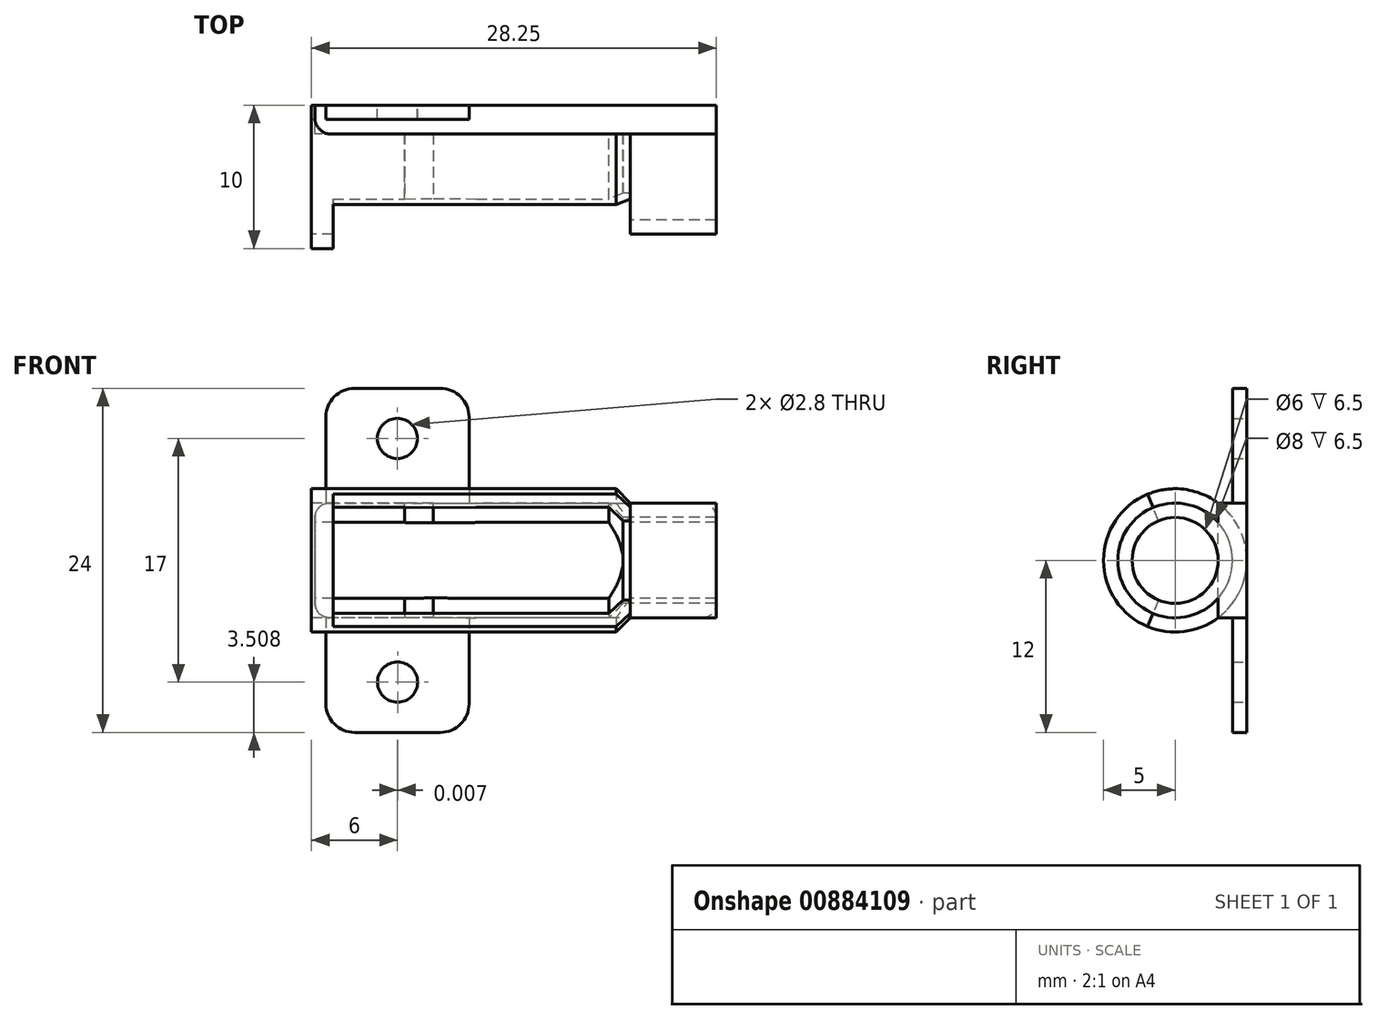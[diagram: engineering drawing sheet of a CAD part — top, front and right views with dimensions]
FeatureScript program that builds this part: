
annotation { "Feature Type Name" : "Feature", "Feature Type Description" : "" }
export const myFeature = defineFeature(function(context is Context, id is Id, definition is map)
    precondition{}
    {
        {
            var Q0;
            Q0=qCreatedBy(makeId("Top.planeOp"),FACE);
            var sketch = newSketch(context, id + "F0", { "sketchPlane" : qUnion([Q0])});
            skLineSegment(sketch, "E0.right", {"start": v(6, 4) * mm, "end": v(6, 3) * mm});
            skLineSegment(sketch, "E1", {"start": v(-8.97, 0) * mm, "end": v(15.16, 0) * mm});
            skLineSegment(sketch, "E2.bottom", {"start": v(-9.75, 5) * mm, "end": v(-19.75, 5) * mm});
            skLineSegment(sketch, "E2.right", {"start": v(-19.75, 5) * mm, "end": v(-19.75, 4) * mm});
            skPoint(sketch, "E3.firstSnap0", {"position": v(-19.75, 4.5) * mm});
            skLineSegment(sketch, "E3.bottom", {"start": v(-19.75, 4) * mm, "end": v(-21.25, 4) * mm});
            skLineSegment(sketch, "E3.top", {"start": v(-19.75, 5) * mm, "end": v(-21.25, 5) * mm});
            skLineSegment(sketch, "E3.left", {"start": v(-19.75, 4) * mm, "end": v(-19.75, 5) * mm});
            skLineSegment(sketch, "E3.right", {"start": v(-21.25, 4) * mm, "end": v(-21.25, 5) * mm});
            skLineSegment(sketch, "E4", {"start": v(-9.75, 5) * mm, "end": v(0, 5) * mm});
            skLineSegment(sketch, "E5", {"start": v(0, 5) * mm, "end": v(1, 4) * mm});
            skLineSegment(sketch, "E6", {"start": v(-9.75, 4) * mm, "end": v(-0.5, 4) * mm});
            skLineSegment(sketch, "E7", {"start": v(0.5, 3) * mm, "end": v(-0.5, 4) * mm});
            skLineSegment(sketch, "E8.bottom", {"start": v(6, 4) * mm, "end": v(7, 4) * mm});
            skLineSegment(sketch, "E8.right", {"start": v(7, 4) * mm, "end": v(7, 3) * mm});
            skLineSegment(sketch, "E9.bottom", {"start": v(1, 4) * mm, "end": v(6, 4) * mm});
            skLineSegment(sketch, "E9.top", {"start": v(1, 3) * mm, "end": v(6, 3) * mm});
            skLineSegment(sketch, "E9.left", {"start": v(1, 4) * mm, "end": v(1, 3) * mm});
            skLineSegment(sketch, "E10", {"start": v(1, 3) * mm, "end": v(0.5, 3) * mm});
            skPoint(sketch, "E11", {"position": v(-14.75, 4) * mm});
            skLineSegment(sketch, "E12", {"start": v(-19.75, 4) * mm, "end": v(-14.75, 4) * mm});
            skLineSegment(sketch, "E13", {"start": v(-9.75, 4) * mm, "end": v(-9.75, 5) * mm});
            skLineSegment(sketch, "E14", {"start": v(6, 3) * mm, "end": v(7, 3) * mm});
            skLineSegment(sketch, "E15", {"start": v(-14.75, 4) * mm, "end": v(-12.75, 3.98) * mm});
            skLineSegment(sketch, "E16", {"start": v(-12.75, 3.98) * mm, "end": v(-9.75, 4) * mm});
            skSolve(sketch);
        }
        {
            var Q0;
            Q0=makeQuery(id+"F0.imprint","IMPRINT",FACE,{"disambiguationData":[TD([[makeQuery(id+"F0.imprint","IMPRINT",EDGE,{"derivedFrom":sQuery(id+"F0.wireOp",EDGE,"E0.bottom")}),-1.0]])]});
            var Q1;
            {var subQ3=sQuery(id+"F0.wireOp",EDGE,"E2.bottom");Q1=makeQuery(id+"F0.imprint","IMPRINT",FACE,{"disambiguationData":[TD([[makeQuery(id+"F0.imprint","IMPRINT",EDGE,{"derivedFrom":subQ3}),1.0]])]});}
            var Q2;
            {var subQ1=sQuery(id+"F0.wireOp",EDGE,"E4");Q2=makeQuery(id+"F0.imprint","IMPRINT",FACE,{"disambiguationData":[TD([[makeQuery(id+"F0.imprint","IMPRINT",EDGE,{"derivedFrom":subQ1}),-1.0]])]});}
            var Q3;
            Q3=sQuery(id+"F0.wireOp",EDGE,"E1");
            revolve(context, id + "F1", {"surfaceOperationType" : NewSurfaceOperationType.NEW, "entities" : qUnion([Q0, Q1, Q2]), "axis" : qUnion([Q3]), "revolveType" : RevolveType.SYMMETRIC, "angle" : 225 * degree});
        }
        {
            var Q0;
            {var subQ3=sQuery(id+"F0.wireOp",EDGE,"E3.bottom");Q0=makeQuery(id+"F0.imprint","IMPRINT",FACE,{"disambiguationData":[TD([[makeQuery(id+"F0.imprint","IMPRINT",EDGE,{"derivedFrom":subQ3}),-1.0]])]});}
            var Q1;
            Q1=makeQuery(id+"F0.imprint","IMPRINT",FACE,{"disambiguationData":[TD([[makeQuery(id+"F0.imprint","IMPRINT",EDGE,{"derivedFrom":sQuery(id+"F0.wireOp",EDGE,"kjC3ubSE-sXcu-RXm1-izS6-ZlQ1TePMqKI2.bottom")}),-1.0]])]});
            var Q2;
            Q2=sQuery(id+"F0.wireOp",EDGE,"E1");
            revolve(context, id + "F2", {"operationType" : NewBodyOperationType.ADD, "surfaceOperationType" : NewSurfaceOperationType.NEW, "entities" : qUnion([Q0, Q1]), "axis" : qUnion([Q2]), "revolveType" : RevolveType.FULL});
        }
        {
            var Q0;
            Q0=makeQuery(id+"F0.imprint","IMPRINT",FACE,{"disambiguationData":[TD([[makeQuery(id+"F0.imprint","IMPRINT",EDGE,{"derivedFrom":sQuery(id+"F0.wireOp",EDGE,"E8.bottom")}),-1.0]])]});
            var Q1;
            Q1=makeQuery(id+"F0.imprint","IMPRINT",FACE,{"disambiguationData":[TD([[makeQuery(id+"F0.imprint","IMPRINT",EDGE,{"derivedFrom":sQuery(id+"F0.wireOp",EDGE,"E9.bottom")}),-1.0]])]});
            var Q2;
            Q2=sQuery(id+"F0.wireOp",EDGE,"E1");
            revolve(context, id + "F3", {"operationType" : NewBodyOperationType.ADD, "surfaceOperationType" : NewSurfaceOperationType.NEW, "entities" : qUnion([Q0, Q1]), "axis" : qUnion([Q2]), "revolveType" : RevolveType.FULL});
        }
        {
            var Q0;
            Q0=qCreatedBy(makeId("Front.planeOp"),FACE);
            cPlane(context, id + "F4", {"entities" : qUnion([Q0]), "cplaneType" : CPlaneType.OFFSET, "offset" : 5 * mm, "oppositeDirection" : true, "width" : 150 * mm, "height" : 150 * mm});
        }
        {
            var Q0;
            Q0=qCreatedBy(id+"F4.planeOp",FACE);
            var sketch = newSketch(context, id + "F5", { "sketchPlane" : qUnion([Q0])});
            skCircle(sketch, "E17", {"center": v(-15.24, -8.5) * mm, "radius": 1.4 * mm});
            skCircle(sketch, "E18", {"center": v(-15.25, 8.5) * mm, "radius": 1.4 * mm});
            skLineSegment(sketch, "E19", {"start": v(-10.25, 10) * mm, "end": v(-10.25, 0) * mm});
            skLineSegment(sketch, "E20", {"start": v(-10.25, 0) * mm, "end": v(-10.25, -10) * mm});
            skLineSegment(sketch, "E21", {"start": v(-18.25, 12) * mm, "end": v(-12.25, 12) * mm});
            skLineSegment(sketch, "E22", {"start": v(-18.24, -12) * mm, "end": v(-12.25, -12) * mm});
            skLineSegment(sketch, "E23", {"start": v(-20.25, 10) * mm, "end": v(-20.25, 0) * mm});
            skLineSegment(sketch, "E24", {"start": v(-20.25, 0) * mm, "end": v(-20.24, -10) * mm});
            skPoint(sketch, "E25.visualSharp", {"position": v(-20.25, 12) * mm});
            skArc(sketch, "E25.filletArc", {"start": v(-18.25, 12) * mm, "mid": v(-19.66, 11.41) * mm, "end": v(-20.25, 10) * mm});
            skPoint(sketch, "E26.visualSharp", {"position": v(-10.25, 12) * mm});
            skArc(sketch, "E26.filletArc", {"start": v(-10.25, 10) * mm, "mid": v(-10.84, 11.41) * mm, "end": v(-12.25, 12) * mm});
            skPoint(sketch, "E27.visualSharp", {"position": v(-10.25, -12) * mm});
            skArc(sketch, "E27.filletArc", {"start": v(-12.25, -12) * mm, "mid": v(-10.84, -11.41) * mm, "end": v(-10.25, -10) * mm});
            skPoint(sketch, "E28.visualSharp", {"position": v(-20.24, -12) * mm});
            skArc(sketch, "E28.filletArc", {"start": v(-20.24, -10) * mm, "mid": v(-19.66, -11.41) * mm, "end": v(-18.24, -12) * mm});
            skSolve(sketch);
        }
        {
            var Q0;
            Q0=qCreatedBy(id+"F4.planeOp",FACE);
            var sketch = newSketch(context, id + "F6", { "sketchPlane" : qUnion([Q0])});
            skLineSegment(sketch, "E29", {"start": v(-20, 4) * mm, "end": v(0, 4) * mm});
            skLineSegment(sketch, "E30", {"start": v(0, 4) * mm, "end": v(6, 4) * mm});
            skLineSegment(sketch, "E31", {"start": v(7, 3) * mm, "end": v(7, 0) * mm});
            skLineSegment(sketch, "E32", {"start": v(7, 0) * mm, "end": v(7, -3) * mm});
            skLineSegment(sketch, "E33", {"start": v(6, -4) * mm, "end": v(0, -4) * mm});
            skLineSegment(sketch, "E34", {"start": v(0, -4) * mm, "end": v(-20, -4) * mm});
            skLineSegment(sketch, "E35", {"start": v(-21, -3) * mm, "end": v(-21, 0) * mm});
            skLineSegment(sketch, "E36", {"start": v(-21, 0) * mm, "end": v(-21, 3) * mm});
            skPoint(sketch, "E37.visualSharp", {"position": v(-21, 4) * mm});
            skArc(sketch, "E37.filletArc", {"start": v(-20, 4) * mm, "mid": v(-20.7, 3.7) * mm, "end": v(-21, 3) * mm});
            skPoint(sketch, "E38.visualSharp", {"position": v(-21, -4) * mm});
            skArc(sketch, "E38.filletArc", {"start": v(-21, -3) * mm, "mid": v(-20.7, -3.7) * mm, "end": v(-20, -4) * mm});
            skPoint(sketch, "E39.visualSharp", {"position": v(7, 4) * mm});
            skArc(sketch, "E39.filletArc", {"start": v(7, 3) * mm, "mid": v(6.7, 3.7) * mm, "end": v(6, 4) * mm});
            skPoint(sketch, "E40.visualSharp", {"position": v(7, -4) * mm});
            skArc(sketch, "E40.filletArc", {"start": v(6, -4) * mm, "mid": v(6.7, -3.7) * mm, "end": v(7, -3) * mm});
            skSolve(sketch);
        }
        {
            var Q0;
            Q0 = qSketchRegion(id + "F6", true);
            extrude(context, id + "F7", {"entities" : qUnion([Q0]), "operationType" : NewBodyOperationType.ADD, "depth" : 2 * mm, "offsetDistance" : 25 * mm});
        }
        {
            var Q0;
            Q0 = qSketchRegion(id + "F5", true);
            extrude(context, id + "F8", {"entities" : qUnion([Q0]), "operationType" : NewBodyOperationType.ADD, "depth" : 1 * mm, "offsetDistance" : 25 * mm});
        }
    });
